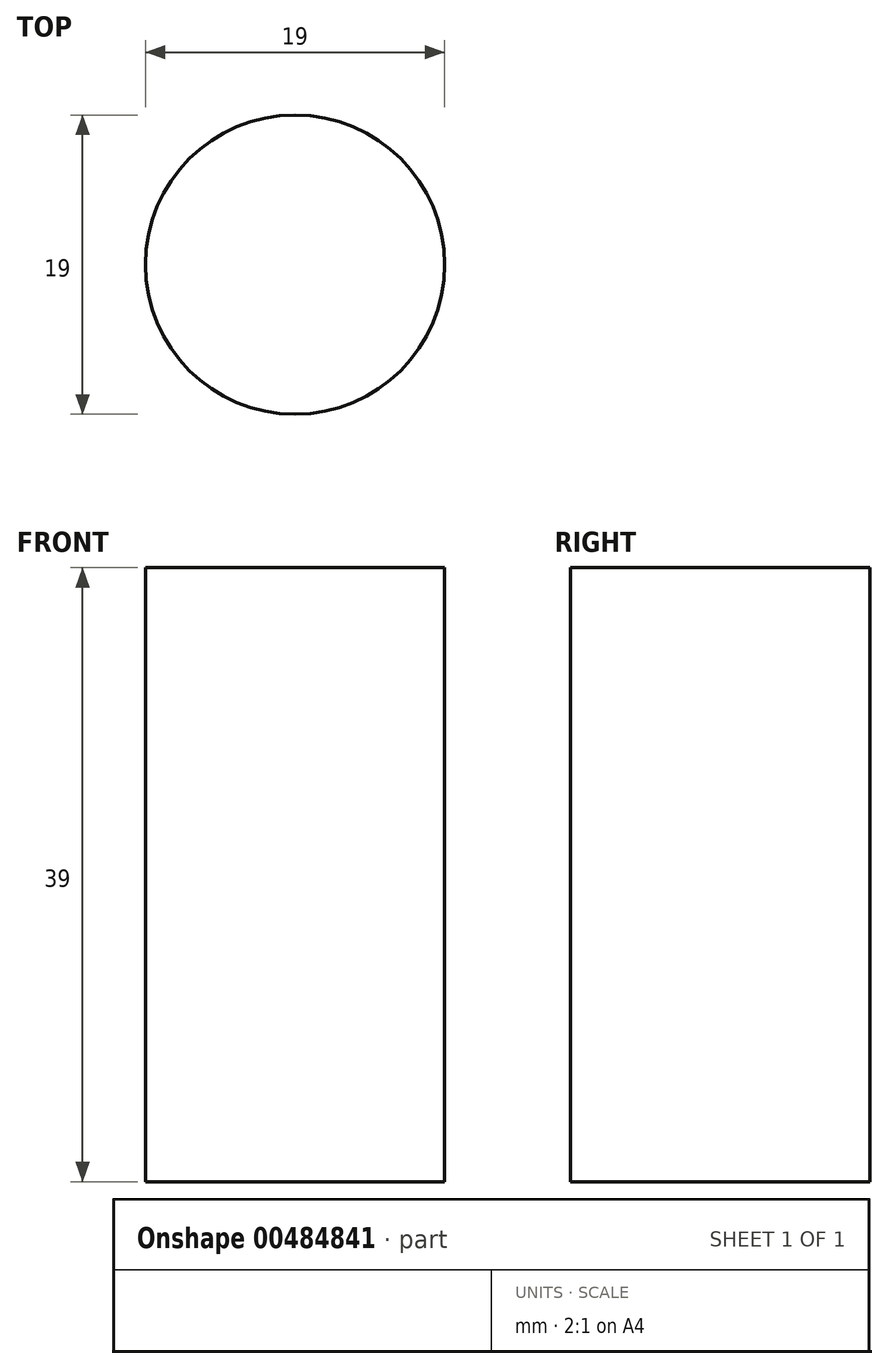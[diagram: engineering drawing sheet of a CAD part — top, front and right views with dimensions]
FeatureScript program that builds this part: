
annotation { "Feature Type Name" : "Feature", "Feature Type Description" : "" }
export const myFeature = defineFeature(function(context is Context, id is Id, definition is map)
    precondition{}
    {
        {
            var Q0;
            Q0=qCreatedBy(makeId("Top.planeOp"),FACE);
            var sketch = newSketch(context, id + "F0", { "sketchPlane" : qUnion([Q0])});
            skCircle(sketch, "E0", {"center": v(0, 0) * mm, "radius": 9.5 * mm});
            skSolve(sketch);
        }
        {
            var Q0;
            Q0 = qSketchRegion(id + "F0", true);
            extrude(context, id + "F1", {"entities" : qUnion([Q0]), "depth" : 39 * mm});
        }
    });
